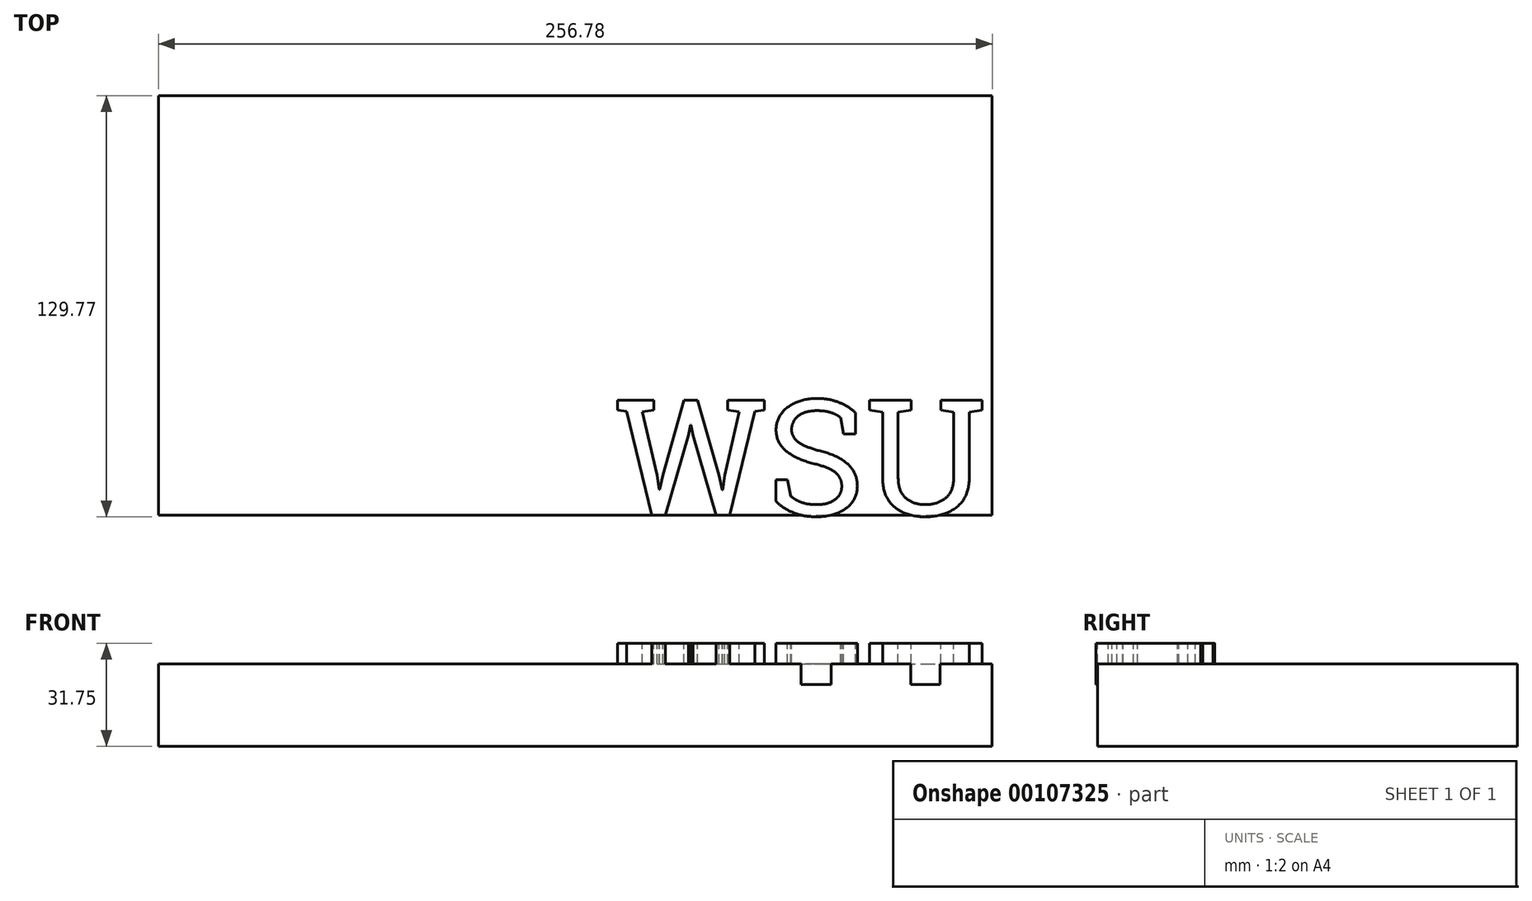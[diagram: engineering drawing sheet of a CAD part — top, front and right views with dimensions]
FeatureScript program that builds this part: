
annotation { "Feature Type Name" : "Feature", "Feature Type Description" : "" }
export const myFeature = defineFeature(function(context is Context, id is Id, definition is map)
    precondition{}
    {
        {
            var Q0;
            Q0=qCreatedBy(makeId("Top.planeOp"),FACE);
            var sketch = newSketch(context, id + "F0", { "sketchPlane" : qUnion([Q0])});
            skLineSegment(sketch, "E0.bottom", {"start": v(-30.38, 85.66) * mm, "end": v(226.4, 85.66) * mm});
            skLineSegment(sketch, "E0.top", {"start": v(-30.38, -43.6) * mm, "end": v(226.4, -43.6) * mm});
            skLineSegment(sketch, "E0.left", {"start": v(-30.38, 85.66) * mm, "end": v(-30.38, -43.6) * mm});
            skLineSegment(sketch, "E0.right", {"start": v(226.4, 85.66) * mm, "end": v(226.4, -43.6) * mm});
            skSolve(sketch);
        }
        {
            var Q0;
            Q0=makeQuery(id+"F0.imprint","IMPRINT",FACE,{"disambiguationData":[TD([[makeQuery(id+"F0.imprint","IMPRINT",EDGE,{"derivedFrom":sQuery(id+"F0.wireOp",EDGE,"E0.bottom")}),-1.0]])]});
            extrude(context, id + "F1", {"entities" : qUnion([Q0]), "depth" : 25.4 * mm});
        }
        {
            var Q0;
            Q0=makeQuery(id+"F1.opExtrude","CAP_FACE",FACE,{"disambiguationData":[OSD([sQuery(id+"F0.wireOp",EDGE,"E0.bottom"),sQuery(id+"F0.wireOp",EDGE,"E0.top"),sQuery(id+"F0.wireOp",EDGE,"E0.left"),sQuery(id+"F0.wireOp",EDGE,"E0.right")])],"isStart":false});
            var sketch = newSketch(context, id + "F2", { "sketchPlane" : qUnion([Q0])});
            skText(sketch, "E1", { "text": "WSU", "fontName": "RobotoSlab-Regular.ttf"});
            const initialGuessF2  = {"E1": [0.11032, -0.0436, 1, 0, 0.03591]};
            skSetInitialGuess(sketch, initialGuessF2);
            skSolve(sketch);
        }
        {
            var Q0;
            Q0=makeQuery(id+"F1.opExtrude","SWEPT_BODY",BODY,{"disambiguationData":[OSD([sQuery(id+"F0.wireOp",EDGE,"E0.bottom"),sQuery(id+"F0.wireOp",EDGE,"E0.top"),sQuery(id+"F0.wireOp",EDGE,"E0.left"),sQuery(id+"F0.wireOp",EDGE,"E0.right")])]});
            transform(context, id + "F3", {"entities" : qUnion([Q0]), "transformType" : TransformType.TRANSLATION_3D, "dx" : 0 * mm, "dy" : 0 * mm, "dz" : -6.35 * mm, "makeCopy" : false});
        }
        {
            var Q0;
            Q0 = qSketchRegion(id + "F2", true);
            extrude(context, id + "F4", {"entities" : qUnion([Q0]), "operationType" : NewBodyOperationType.ADD, "oppositeDirection" : true, "depth" : 12.7 * mm});
        }
    });
